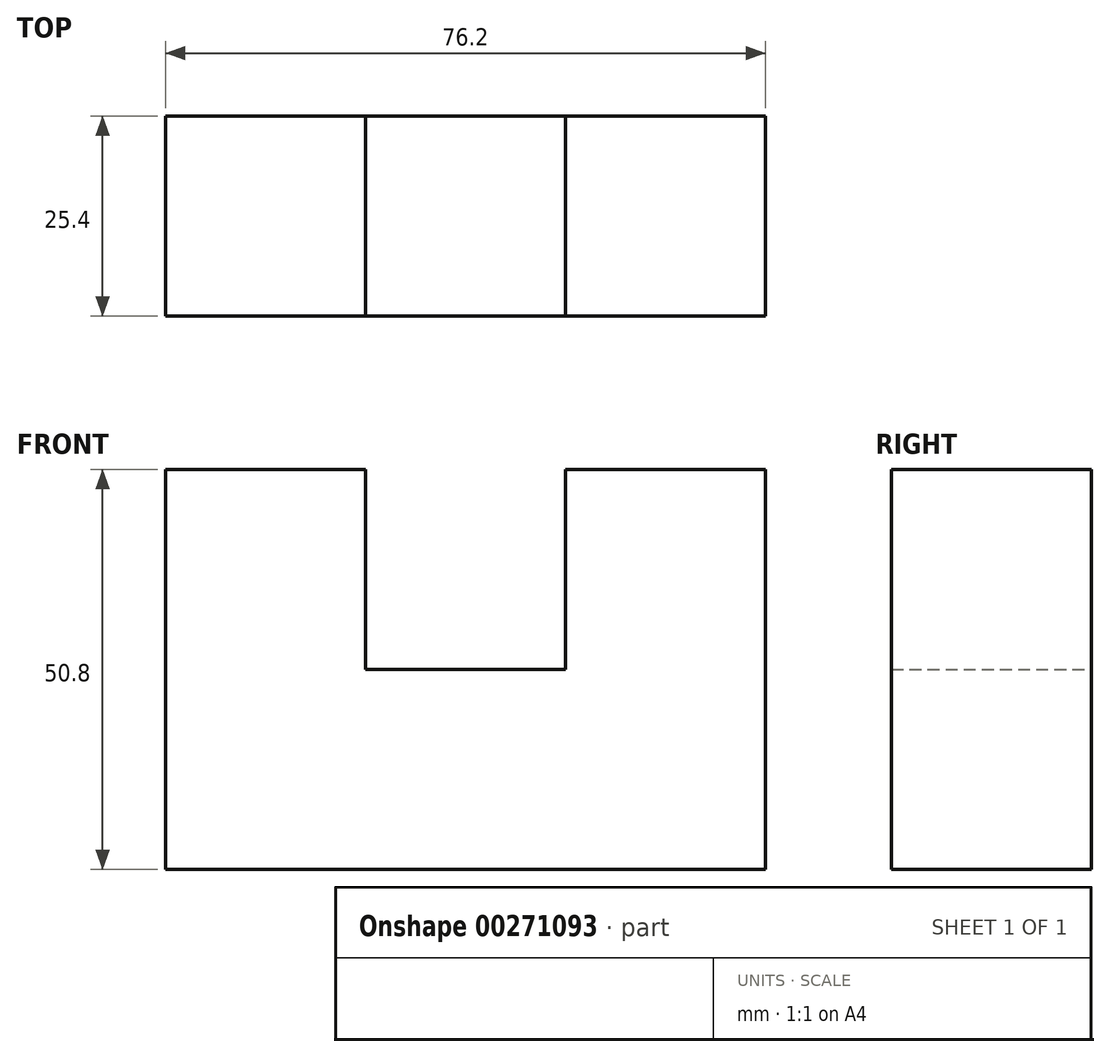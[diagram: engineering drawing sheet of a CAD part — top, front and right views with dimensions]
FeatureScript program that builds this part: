
annotation { "Feature Type Name" : "Feature", "Feature Type Description" : "" }
export const myFeature = defineFeature(function(context is Context, id is Id, definition is map)
    precondition{}
    {
        {
            var Q0;
            Q0=qCreatedBy(makeId("Front.planeOp"),FACE);
            var sketch = newSketch(context, id + "F0", { "sketchPlane" : qUnion([Q0])});
            skLineSegment(sketch, "E0", {"start": v(0, 0) * mm, "end": v(0, -50.8) * mm});
            skLineSegment(sketch, "E1", {"start": v(0, -50.8) * mm, "end": v(76.2, -50.8) * mm});
            skLineSegment(sketch, "E2", {"start": v(76.2, -50.8) * mm, "end": v(76.2, 0) * mm});
            skLineSegment(sketch, "E3", {"start": v(76.2, 0) * mm, "end": v(50.8, 0) * mm});
            skLineSegment(sketch, "E4", {"start": v(50.8, 0) * mm, "end": v(50.8, -25.4) * mm});
            skLineSegment(sketch, "E5", {"start": v(50.8, -25.4) * mm, "end": v(25.4, -25.4) * mm});
            skLineSegment(sketch, "E6", {"start": v(25.4, -25.4) * mm, "end": v(25.4, 0) * mm});
            skLineSegment(sketch, "E7", {"start": v(25.4, 0) * mm, "end": v(0, 0) * mm});
            skSolve(sketch);
        }
        {
            var Q0;
            Q0 = qSketchRegion(id + "F0", true);
            extrude(context, id + "F1", {"entities" : qUnion([Q0]), "depth" : 25.4 * mm});
        }
    });
